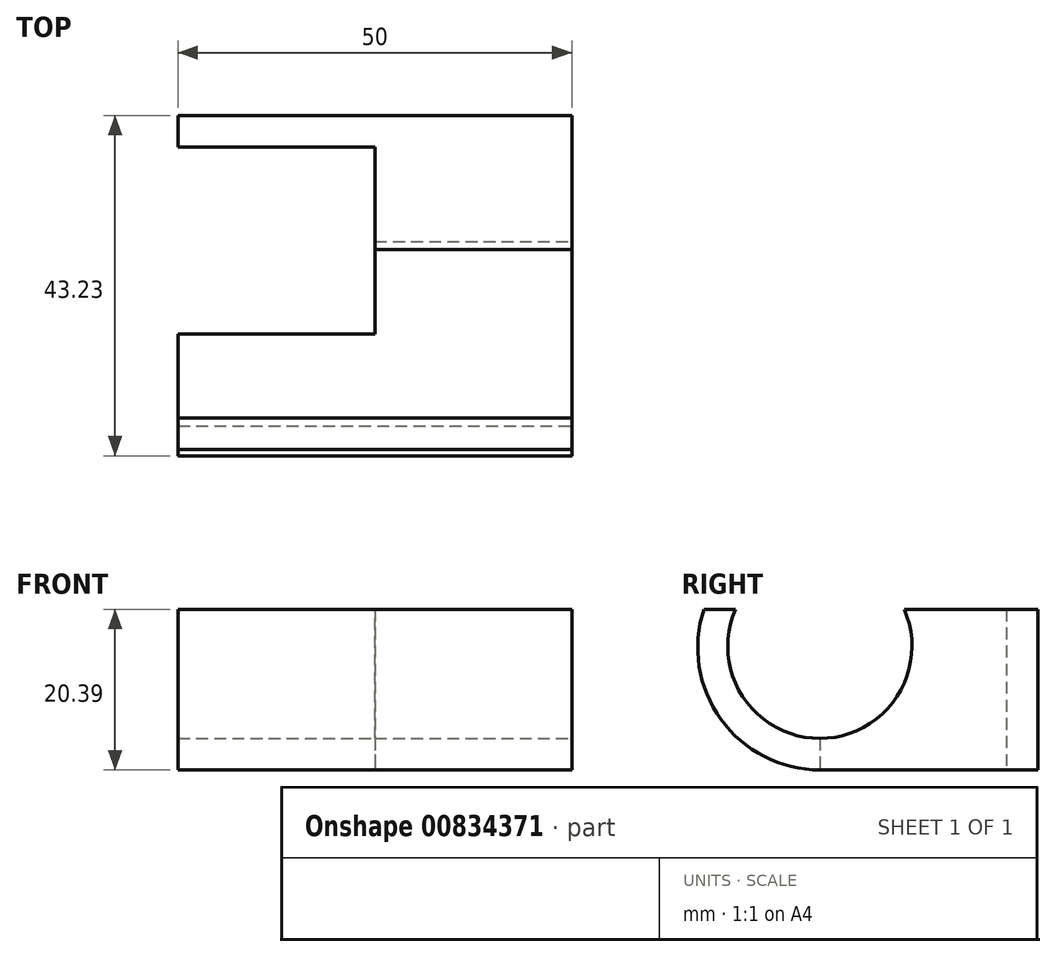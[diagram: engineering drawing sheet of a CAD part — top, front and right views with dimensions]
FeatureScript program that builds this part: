
annotation { "Feature Type Name" : "Feature", "Feature Type Description" : "" }
export const myFeature = defineFeature(function(context is Context, id is Id, definition is map)
    precondition{}
    {
        {
            var Q0;
            Q0=qCreatedBy(makeId("Right.planeOp"),FACE);
            var sketch = newSketch(context, id + "F0", { "sketchPlane" : qUnion([Q0])});
            skCircle(sketch, "E0", {"center": v(-1.32, 0) * mm, "radius": 11.7 * mm});
            skLineSegment(sketch, "E1", {"start": v(-12.04, 4.7) * mm, "end": v(9.4, 4.7) * mm});
            skLineSegment(sketch, "E2", {"start": v(-12.04, 4.7) * mm, "end": v(-16.04, 4.7) * mm});
            skLineSegment(sketch, "E3", {"start": v(9.4, 4.7) * mm, "end": v(13.4, 4.7) * mm});
            skLineSegment(sketch, "E4", {"start": v(-1.32, -11.7) * mm, "end": v(-1.32, -15.7) * mm});
            skArc(sketch, "E5", {"start": v(-16.04, 4.7) * mm, "mid": v(-1.32, -15.7) * mm, "end": v(13.4, 4.7) * mm});
            skLineSegment(sketch, "E6", {"start": v(-1.32, -15.7) * mm, "end": v(26.4, -15.7) * mm});
            skLineSegment(sketch, "E7", {"start": v(13.4, 4.7) * mm, "end": v(22.4, 4.7) * mm});
            skLineSegment(sketch, "E8", {"start": v(22.4, 4.7) * mm, "end": v(26.4, 4.7) * mm});
            skLineSegment(sketch, "E9", {"start": v(22.4, 4.7) * mm, "end": v(22.4, -15.7) * mm});
            skLineSegment(sketch, "E10", {"start": v(26.4, 4.7) * mm, "end": v(26.4, -15.7) * mm});
            skSolve(sketch);
        }
        {
            var Q0;
            {var subQ0=sQuery(id+"F0.wireOp",EDGE,"E3");Q0=makeQuery(id+"F0.imprint","IMPRINT",FACE,{"disambiguationData":[TD([[makeQuery(id+"F0.imprint","IMPRINT",EDGE,{"derivedFrom":subQ0}),-1.0]])]});}
            var Q1;
            {var subQ0=sQuery(id+"F0.wireOp",EDGE,"E7");Q1=makeQuery(id+"F0.imprint","IMPRINT",FACE,{"disambiguationData":[TD([[makeQuery(id+"F0.imprint","IMPRINT",EDGE,{"derivedFrom":subQ0}),-1.0]])]});}
            extrude(context, id + "F1", {"entities" : qUnion([Q0, Q1]), "oppositeDirection" : true, "depth" : 25 * mm, "offsetDistance" : 25 * mm});
        }
        {
            var Q0;
            {var subQ0=sQuery(id+"F0.wireOp",EDGE,"E2");Q0=makeQuery(id+"F0.imprint","IMPRINT",FACE,{"disambiguationData":[TD([[makeQuery(id+"F0.imprint","IMPRINT",EDGE,{"derivedFrom":subQ0}),1.0]])]});}
            extrude(context, id + "F2", {"entities" : qUnion([Q0]), "operationType" : NewBodyOperationType.ADD, "oppositeDirection" : true, "depth" : 50 * mm, "offsetDistance" : 25 * mm});
        }
        {
            var Q0;
            Q0=makeQuery(id+"F0.imprint","IMPRINT",FACE,{"disambiguationData":[TD([[makeQuery(id+"F0.imprint","IMPRINT",EDGE,{"derivedFrom":sQuery(id+"F0.wireOp",EDGE,"E8")}),-1.0]])]});
            extrude(context, id + "F3", {"entities" : qUnion([Q0]), "operationType" : NewBodyOperationType.ADD, "oppositeDirection" : true, "depth" : 50 * mm, "offsetDistance" : 25 * mm});
        }
        {
            var Q0;
            Q0=makeQuery(id+"F1.opExtrude","SWEPT_BODY",BODY,{"disambiguationData":[OSD([sQuery(id+"F0.wireOp",EDGE,"E0"),sQuery(id+"F0.wireOp",EDGE,"E3"),sQuery(id+"F0.wireOp",EDGE,"E4"),sQuery(id+"F0.wireOp",EDGE,"E6"),sQuery(id+"F0.wireOp",EDGE,"E7"),sQuery(id+"F0.wireOp",EDGE,"E9")])]});
            transform(context, id + "F4", {"entities" : qUnion([Q0]), "transformType" : TransformType.TRANSLATION_3D, "dx" : 0 * mm, "dy" : 0 * mm, "dz" : 0 * mm, "makeCopy" : true});
        }
        {
            var Q0;
            Q0=makeQuery(id+"F4.opPattern","COPY",BODY,{"derivedFrom":makeQuery(id+"F1.opExtrude","SWEPT_BODY",BODY,{"disambiguationData":[OSD([sQuery(id+"F0.wireOp",EDGE,"E0"),sQuery(id+"F0.wireOp",EDGE,"E3"),sQuery(id+"F0.wireOp",EDGE,"E4"),sQuery(id+"F0.wireOp",EDGE,"E6"),sQuery(id+"F0.wireOp",EDGE,"E7"),sQuery(id+"F0.wireOp",EDGE,"E9")])]}),"instanceName":"1"});
            var Q1;
            {var subQ0=sQuery(id+"F0.wireOp",EDGE,"E1");Q1=makeQuery(id+"F0.imprint","IMPRINT",FACE,{"disambiguationData":[TD([[makeQuery(id+"F0.imprint","IMPRINT",EDGE,{"derivedFrom":subQ0}),-1.0]])]});}
            mirror(context, id + "F5", {"entities" : qUnion([Q0]), "mirrorPlane" : qUnion([Q1])});
        }
        {
            var Q0;
            Q0=makeQuery(id+"F4.opPattern","COPY",BODY,{"derivedFrom":makeQuery(id+"F1.opExtrude","SWEPT_BODY",BODY,{"disambiguationData":[OSD([sQuery(id+"F0.wireOp",EDGE,"E0"),sQuery(id+"F0.wireOp",EDGE,"E3"),sQuery(id+"F0.wireOp",EDGE,"E4"),sQuery(id+"F0.wireOp",EDGE,"E6"),sQuery(id+"F0.wireOp",EDGE,"E7"),sQuery(id+"F0.wireOp",EDGE,"E9")])]}),"instanceName":"1"});
            deleteBodies(context, id + "F6", {"entities" : qUnion([Q0])});
        }
        {
            var Q0;
            Q0=makeQuery(id+"F5.opPattern","COPY",BODY,{"derivedFrom":makeQuery(id+"F4.opPattern","COPY",BODY,{"derivedFrom":makeQuery(id+"F1.opExtrude","SWEPT_BODY",BODY,{"disambiguationData":[OSD([sQuery(id+"F0.wireOp",EDGE,"E0"),sQuery(id+"F0.wireOp",EDGE,"E3"),sQuery(id+"F0.wireOp",EDGE,"E4"),sQuery(id+"F0.wireOp",EDGE,"E6"),sQuery(id+"F0.wireOp",EDGE,"E7"),sQuery(id+"F0.wireOp",EDGE,"E9")])]}),"instanceName":"1"}),"instanceName":"1"});
            deleteBodies(context, id + "F7", {"entities" : qUnion([Q0])});
        }
    });
